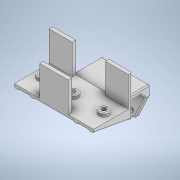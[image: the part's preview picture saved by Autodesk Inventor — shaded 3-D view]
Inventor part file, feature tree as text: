
AUTODESK INVENTOR PART (.ipt)
format: ipt  version: 2020 (Build 240168000, 168)  size: 463,872 bytes
history: native  units: in
note: dims shown in document units (in); Inventor stores cm internally (conversion verified against a paired STEP export)
features: extrude x18, sketch x18, fillet x4
ambient origin geometry x8: Origin, YZ Plane, XZ Plane, XY Plane, X Axis, Y Axis, Z Axis, Center Point
bodies: Solid1 (feature_tree)
feature tree (40):
  extrude  "Extrusion1"  Depth=1.2756in
  extrude  "Extrusion3"  Depth=0.1181in
  extrude  "Extrusion4"  Depth=1.0in TaperAngle=0.0deg
  extrude  "Extrusion5"  Depth=0.1181in TaperAngle=0.0deg
  extrude  "Extrusion6"  Depth=0.1181in TaperAngle=0.0deg
  extrude  "Extrusion9"  Depth=0.3346in
  extrude  "Extrusion10"  Depth=1.0236in
  extrude  "Extrusion11"  Depth=0.2953in
  extrude  "Extrusion14"  Depth=0.3346in
  fillet  "Fillet1"  Radius=0.1181in
  extrude  "Extrusion15"  Depth=0.1181in
  extrude  "Extrusion16"  Depth=0.1772in TaperAngle=0.0deg
  extrude  "Extrusion17"  Depth=0.0394in
  extrude  "Extrusion18"  Depth=0.1575in
  extrude  "Extrusion19"  Depth=0.3937in
  extrude  "Extrusion20"  Depth=0.2362in
  extrude  "Extrusion21"  Depth=0.1575in
  extrude  "Extrusion22"  Depth=0.1575in
  extrude  "Extrusion23"  Depth=0.0394in
  fillet  "Fillet3"  Radius=0.1575in
  fillet  "Fillet4"  Radius=0.5118in
  fillet  "Fillet5"  Radius=1.1181in
  sketch  "Sketch1"  dims[d0=1.6142in d1=1.2756in]
  sketch  "Sketch3"  dims[d2=0.1181in d3=0.0in d8=0.1181in]
  sketch  "Sketch4"  dims[d9=0.1181in d10=1.0in d11=0.0in]
  sketch  "Sketch5"  dims[d12=0.8465in d13=0.1181in d14=0.0in]
  sketch  "Sketch6"  dims[d15=0.8465in d16=0.1181in d17=0.0in]
  sketch  "Sketch9"  dims[d20=0.3346in d21=0.3346in]
  sketch  "Sketch10"  dims[d22=0.1181in d23=0.0in d32=1.0236in]
  sketch  "Sketch11"  dims[d33=0.2953in d34=0.2953in]
  sketch  "Sketch14"  dims[d35=1.0236in d36=0.0in d37=0.3346in d38=0.1181in d39=0.0in]
  sketch  "Sketch15"  dims[d40=0.7677in d41=0.1181in]
  sketch  "Sketch16"  dims[d42=1.0in d43=0.0in d50=0.1772in d51=0.0in]
  sketch  "Sketch17"  dims[d52=0.0394in d54=0.1575in]
  sketch  "Sketch18"  dims[d55=0.1575in d56=0.1575in]
  sketch  "Sketch19"  dims[d57=0.3937in d58=0.0in d59=0.2362in]
  sketch  "Sketch20"  dims[d60=0.2362in d61=0.2362in]
  sketch  "Sketch21"  dims[d62=0.1181in d63=0.0in d64=0.1575in]
  sketch  "Sketch22"  dims[d65=0.1575in d66=0.1575in]
  sketch  "Sketch23"  dims[d67=0.1969in d68=0.0in d69=1.6142in d70=0.1575in d71=0.5118in d72=1.1181in d73=0.0in d74=0.1575in d75=0.1575in d76=0.1969in d77=0.0in d78=0.1575in d79=0.937in d80=0.0in d81=0.1575in d82=0.1575in d83=0.1575in d84=0.1575in d85=0.1575in d86=0.0in d87=0.4331in d88=0.5512in d89=0.1575in d90=0.1575in d91=0.4466in d92=0.7902in d93=0.1575in d94=0.0in d95=2.6378in d96=0.0in d97=0.1181in d98=0.0394in d99=0.0394in d44=0.0197in d45=0.0344in]
